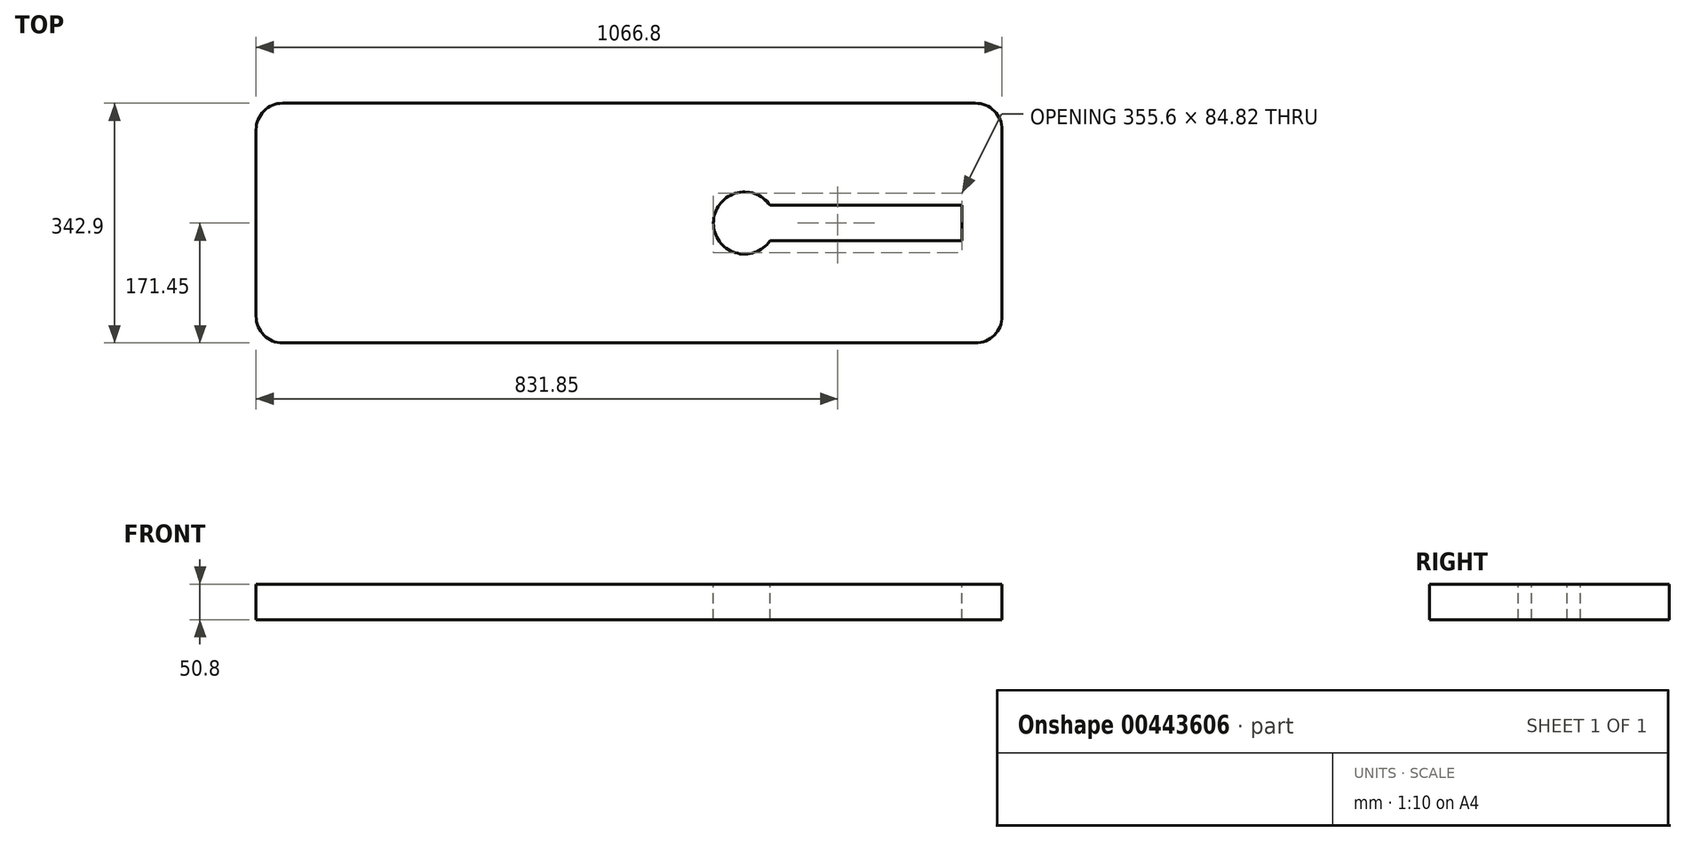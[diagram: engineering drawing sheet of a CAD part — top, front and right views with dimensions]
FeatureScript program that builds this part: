
annotation { "Feature Type Name" : "Feature", "Feature Type Description" : "" }
export const myFeature = defineFeature(function(context is Context, id is Id, definition is map)
    precondition{}
    {
        {
            var Q0;
            Q0=qCreatedBy(makeId("Top.planeOp"),FACE);
            var sketch = newSketch(context, id + "F0", { "sketchPlane" : qUnion([Q0])});
            skLineSegment(sketch, "E0.bottom", {"start": v(533.4, -171.45) * mm, "end": v(-533.4, -171.45) * mm});
            skLineSegment(sketch, "E0.top", {"start": v(533.4, 171.45) * mm, "end": v(-533.4, 171.45) * mm});
            skLineSegment(sketch, "E0.left", {"start": v(533.4, -171.45) * mm, "end": v(533.4, 171.45) * mm});
            skLineSegment(sketch, "E0.right", {"start": v(-533.4, -171.45) * mm, "end": v(-533.4, 171.45) * mm});
            skPoint(sketch, "E0.middle", {"position": v(0, 0) * mm});
            skSolve(sketch);
        }
        {
            var Q0;
            Q0=qSketchRegion(id+"F0",true);
            extrude(context, id + "F1", {"entities" : qUnion([Q0]), "depth" : 50.8 * mm});
        }
        {
            var Q0;
            Q0=makeQuery(id+"F1.opExtrude","SWEPT_EDGE",EDGE,{"disambiguationData":[OSD([sQuery(id+"F0.wireOp",EDGE,"E0.top"),sQuery(id+"F0.wireOp",EDGE,"E0.right")])]});
            var Q1;
            Q1=makeQuery(id+"F1.opExtrude","SWEPT_EDGE",EDGE,{"disambiguationData":[OSD([sQuery(id+"F0.wireOp",EDGE,"E0.bottom"),sQuery(id+"F0.wireOp",EDGE,"E0.right")])]});
            var Q2;
            Q2=makeQuery(id+"F1.opExtrude","SWEPT_EDGE",EDGE,{"disambiguationData":[OSD([sQuery(id+"F0.wireOp",EDGE,"E0.top"),sQuery(id+"F0.wireOp",EDGE,"E0.left")])]});
            var Q3;
            Q3=makeQuery(id+"F1.opExtrude","SWEPT_EDGE",EDGE,{"disambiguationData":[OSD([sQuery(id+"F0.wireOp",EDGE,"E0.bottom"),sQuery(id+"F0.wireOp",EDGE,"E0.left")])]});
            fillet(context, id + "F2", {"entities" : qUnion([Q0, Q1, Q2, Q3]), "radius" : 38.1 * mm, "tangentPropagation" : true, "allowEdgeOverflow" : false});
        }
        {
            var Q0;
            Q0=makeQuery(id+"F1.opExtrude","CAP_FACE",FACE,{"disambiguationData":[OSD([sQuery(id+"F0.wireOp",EDGE,"E0.bottom"),sQuery(id+"F0.wireOp",EDGE,"E0.top"),sQuery(id+"F0.wireOp",EDGE,"E0.left"),sQuery(id+"F0.wireOp",EDGE,"E0.right")])],"isStart":false});
            var sketch = newSketch(context, id + "F3", { "sketchPlane" : qUnion([Q0])});
            skCircle(sketch, "E1", {"center": v(165.1, 0) * mm, "radius": 44.45 * mm});
            skLineSegment(sketch, "E2", {"start": v(201.58, 25.4) * mm, "end": v(476.25, 25.4) * mm});
            skLineSegment(sketch, "E3", {"start": v(476.25, 25.4) * mm, "end": v(476.25, -25.4) * mm});
            skLineSegment(sketch, "E4", {"start": v(476.25, -25.4) * mm, "end": v(201.58, -25.4) * mm});
            skSolve(sketch);
        }
        {
            var Q0;
            Q0 = qSketchRegion(id + "F3", true);
            extrude(context, id + "F4", {"entities" : qUnion([Q0]), "operationType" : NewBodyOperationType.REMOVE, "oppositeDirection" : true, "depth" : 50.8 * mm});
        }
    });
